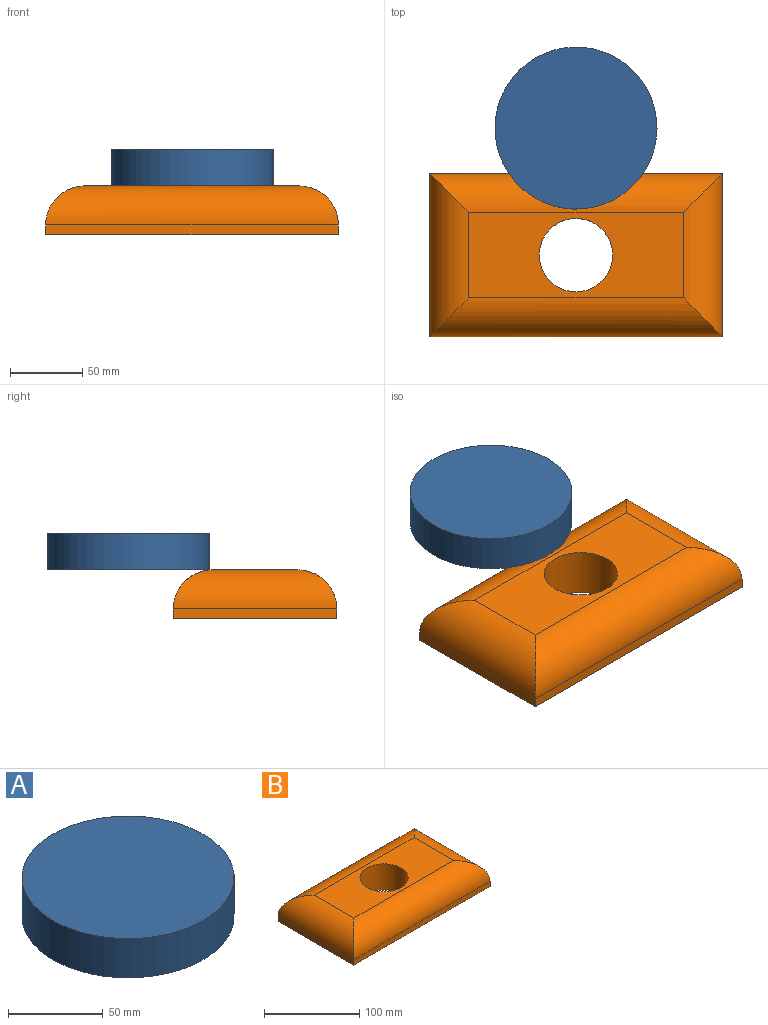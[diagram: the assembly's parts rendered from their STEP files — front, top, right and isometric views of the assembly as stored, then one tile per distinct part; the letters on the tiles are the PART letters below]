
ASSEMBLY  parts=2 mates=1
PART A: 3 faces, bbox 112.1x112.1x25.4 mm
  f0: cylinder r=56.06mm len=112.13mm, axis (0,0,-1), area 8947.5mm2, adj f1,f2
  f1: plane 112.13x112.13mm, normal (0,0,1), area 9874.7mm2, adj f0
  f2: plane 112.13x112.13mm, normal (0,0,-1), area 9874.7mm2, adj f0
PART B: 11 faces, bbox 202.5x113x33.8 mm
  f0: plane 202.48x6.8mm, normal (0,-1,0), area 1377mm2, adj f1,f3,f5,f6
  f1: plane 113.04x6.8mm, normal (1,0,0), area 768.7mm2, adj f0,f2,f5,f7
  f2: plane 202.48x6.8mm, normal (0,1,0), area 1377mm2, adj f1,f3,f5,f9
  f3: plane 113.04x6.8mm, normal (-1,0,0), area 768.7mm2, adj f0,f2,f5,f8
  f4: plane 148.52x59.07mm, normal (0,0,1), area 6746.7mm2, adj f6,f7,f8,f9,f10
  f5: plane 202.48x113.04mm, normal (0,0,-1), area 20860.9mm2, adj f0,f1,f2,f3,f10
  f6: cylinder r=26.98mm len=202.48mm, axis (-1,0,0), area 7750.6mm2, adj f0,f4,f7,f8
  f7: cylinder r=26.98mm len=113.04mm, axis (0,-1,0), area 3959.6mm2, adj f1,f4,f6,f9
  f8: cylinder r=26.98mm len=113.04mm, axis (0,1,0), area 3959.6mm2, adj f3,f4,f6,f9
  f9: cylinder r=26.98mm len=202.48mm, axis (1,0,0), area 7750.6mm2, adj f2,f4,f7,f8
  f10: cylinder r=25.4mm len=50.8mm, axis (0,0,1), area 5391.4mm2, adj f4,f5
PLACE A t=(34.31,160.09,56.8)mm
PLACE B t=(34.31,66.14,23.02)mm
MATE planar B.f10 <-> A.f0  axis (0,0,1) through (34.31,66.14,56.8)mm
